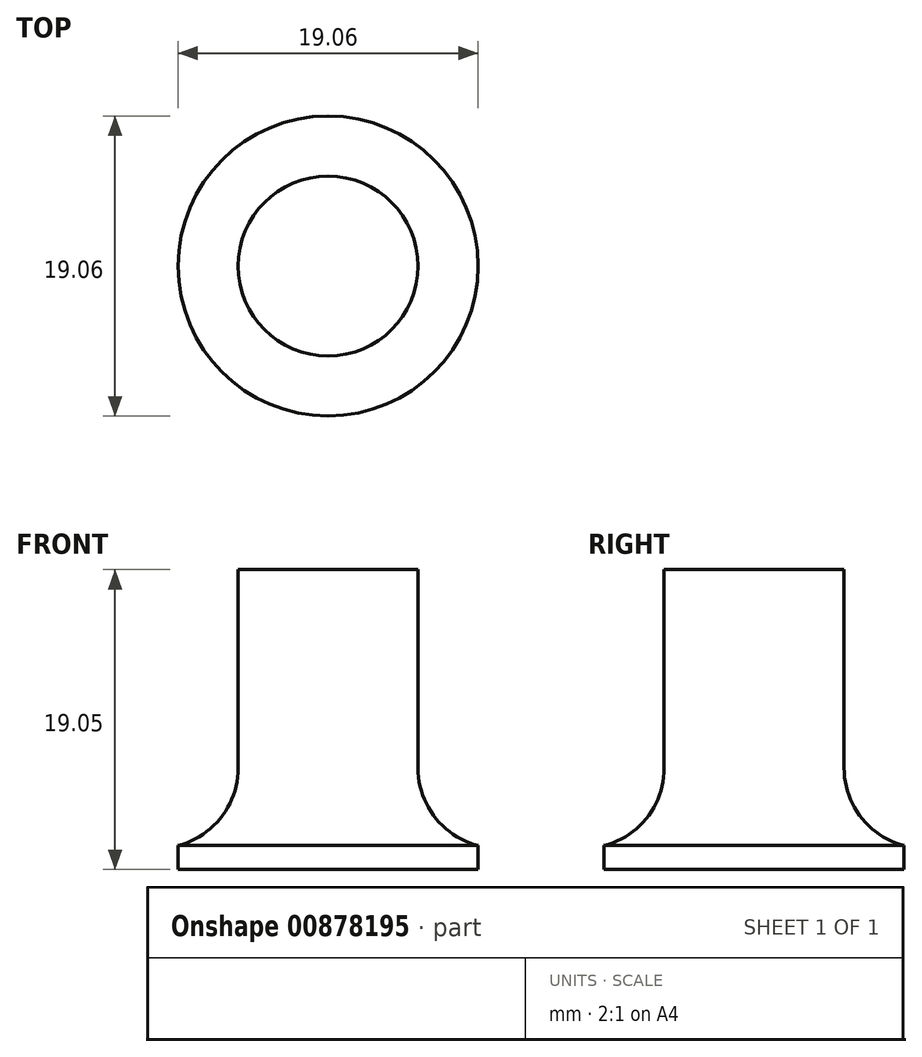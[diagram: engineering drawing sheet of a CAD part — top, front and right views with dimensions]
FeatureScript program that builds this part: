
annotation { "Feature Type Name" : "Feature", "Feature Type Description" : "" }
export const myFeature = defineFeature(function(context is Context, id is Id, definition is map)
    precondition{}
    {
        {
            var Q0;
            Q0=qCreatedBy(makeId("Front.planeOp"),FACE);
            var sketch = newSketch(context, id + "F0", { "sketchPlane" : qUnion([Q0])});
            skLineSegment(sketch, "E0.bottom", {"start": v(0, 0) * mm, "end": v(-9.53, 0) * mm});
            skLineSegment(sketch, "E0.top", {"start": v(0, 1.52) * mm, "end": v(-9.53, 1.52) * mm});
            skLineSegment(sketch, "E0.left", {"start": v(0, 0) * mm, "end": v(0, 1.52) * mm});
            skLineSegment(sketch, "E0.right", {"start": v(-9.53, 0) * mm, "end": v(-9.53, 1.52) * mm});
            skSolve(sketch);
        }
        {
            var Q0;
            Q0 = qSketchRegion(id + "F0", true);
            var Q1;
            Q1=sQuery(id+"F0.wireOp",EDGE,"E0.left");
            revolve(context, id + "F1", {"surfaceOperationType" : NewSurfaceOperationType.NEW, "entities" : qUnion([Q0]), "axis" : qUnion([Q1]), "revolveType" : RevolveType.FULL});
        }
        {
            var Q0;
            Q0=qCreatedBy(makeId("Front.planeOp"),FACE);
            var sketch = newSketch(context, id + "F2", { "sketchPlane" : qUnion([Q0])});
            skLineSegment(sketch, "E1.bottom", {"start": v(0, 0) * mm, "end": v(-5.72, 0) * mm});
            skLineSegment(sketch, "E1.top", {"start": v(0, 19.05) * mm, "end": v(-5.72, 19.05) * mm});
            skLineSegment(sketch, "E1.left", {"start": v(0, 0) * mm, "end": v(0, 19.05) * mm});
            skLineSegment(sketch, "E1.right", {"start": v(-5.72, 0) * mm, "end": v(-5.72, 19.05) * mm});
            skSolve(sketch);
        }
        {
            var Q0;
            Q0=makeQuery(id+"F2.imprint","IMPRINT",FACE,{"disambiguationData":[TD([[makeQuery(id+"F2.imprint","IMPRINT",EDGE,{"derivedFrom":sQuery(id+"F2.wireOp",EDGE,"E1.bottom")}),-1.0]])]});
            var Q1;
            Q1=sQuery(id+"F2.wireOp",EDGE,"E1.left");
            revolve(context, id + "F3", {"operationType" : NewBodyOperationType.ADD, "surfaceOperationType" : NewSurfaceOperationType.NEW, "entities" : qUnion([Q0]), "axis" : qUnion([Q1]), "revolveType" : RevolveType.FULL});
        }
        {
            var Q0;
            Q0=makeQuery(id+"F3.boolean.opBoolean","INTERSECT",EDGE,{"derivedFrom":[makeQuery(id+"F1.opRevolve","SWEPT_FACE",FACE,{"disambiguationData":[OSD([sQuery(id+"F0.wireOp",EDGE,"E0.top")])]}),makeQuery(id+"F3.opRevolve","SWEPT_FACE",FACE,{"disambiguationData":[OSD([sQuery(id+"F2.wireOp",EDGE,"E1.right")])]})]});
            fillet(context, id + "F4", {"entities" : qUnion([Q0]), "radius" : 5.08 * mm, "tangentPropagation" : true, "allowEdgeOverflow" : false});
        }
    });
